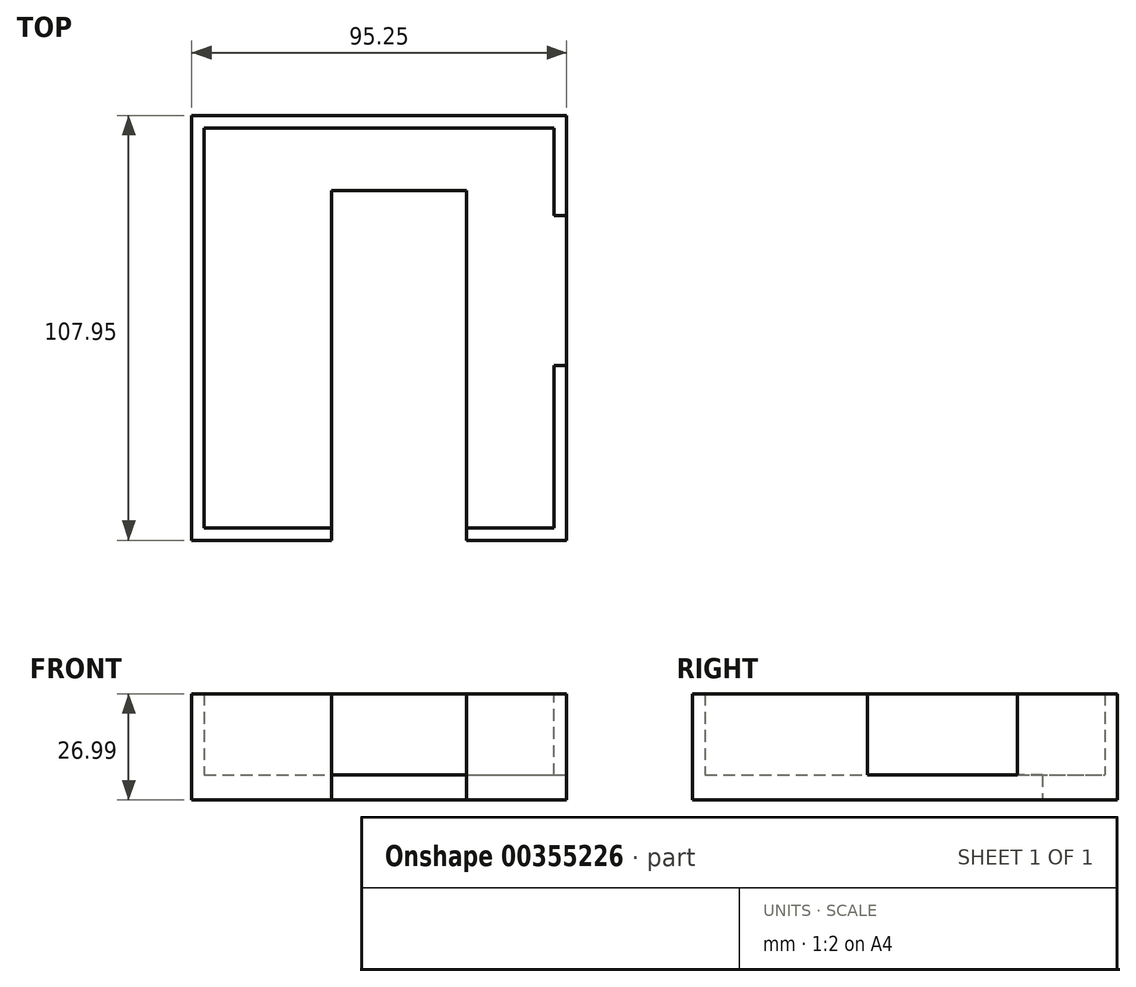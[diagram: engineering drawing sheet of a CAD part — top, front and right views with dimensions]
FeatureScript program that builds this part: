
annotation { "Feature Type Name" : "Feature", "Feature Type Description" : "" }
export const myFeature = defineFeature(function(context is Context, id is Id, definition is map)
    precondition{}
    {
        {
            var Q0;
            Q0=qCreatedBy(makeId("Top.planeOp"),FACE);
            var sketch = newSketch(context, id + "F0", { "sketchPlane" : qUnion([Q0])});
            skLineSegment(sketch, "E0.bottom", {"start": v(-35.56, 52.15) * mm, "end": v(59.7, 52.15) * mm});
            skLineSegment(sketch, "E0.top", {"start": v(-35.56, -55.8) * mm, "end": v(0, -55.8) * mm});
            skLineSegment(sketch, "E0.left", {"start": v(-35.56, 52.15) * mm, "end": v(-35.56, -55.8) * mm});
            skLineSegment(sketch, "E0.right", {"start": v(59.7, 52.15) * mm, "end": v(59.7, -55.8) * mm});
            skPoint(sketch, "E0.middle", {"position": v(12.07, -1.83) * mm});
            skLineSegment(sketch, "E1", {"start": v(34.3, -55.8) * mm, "end": v(34.3, 33.1) * mm});
            skLineSegment(sketch, "E2", {"start": v(34.3, 33.1) * mm, "end": v(0, 33.1) * mm});
            skLineSegment(sketch, "E3", {"start": v(0, 33.1) * mm, "end": v(0, -55.8) * mm});
            skLineSegment(sketch, "E4.trimOffspring", {"start": v(34.3, -55.8) * mm, "end": v(59.7, -55.8) * mm});
            skSolve(sketch);
        }
        {
            var Q0;
            Q0=makeQuery(id+"F0.imprint","IMPRINT",FACE,{"disambiguationData":[TD([[makeQuery(id+"F0.imprint","IMPRINT",EDGE,{"derivedFrom":sQuery(id+"F0.wireOp",EDGE,"E0.bottom")}),-1.0]])]});
            extrude(context, id + "F1", {"entities" : qUnion([Q0]), "depth" : 6.35 * mm});
        }
        {
            var Q0;
            Q0=makeQuery(id+"F1.opExtrude","CAP_FACE",FACE,{"disambiguationData":[OSD([sQuery(id+"F0.wireOp",EDGE,"E0.bottom"),sQuery(id+"F0.wireOp",EDGE,"E0.top"),sQuery(id+"F0.wireOp",EDGE,"E0.left"),sQuery(id+"F0.wireOp",EDGE,"E0.right"),sQuery(id+"F0.wireOp",EDGE,"E1"),sQuery(id+"F0.wireOp",EDGE,"E2"),sQuery(id+"F0.wireOp",EDGE,"E3"),sQuery(id+"F0.wireOp",EDGE,"E4.trimOffspring")])],"isStart":false});
            var sketch = newSketch(context, id + "F2", { "sketchPlane" : qUnion([Q0])});
            skLineSegment(sketch, "E5", {"start": v(0, -55.8) * mm, "end": v(-35.56, -55.8) * mm});
            skLineSegment(sketch, "E6", {"start": v(-35.56, -55.8) * mm, "end": v(-35.56, 52.15) * mm});
            skLineSegment(sketch, "E7", {"start": v(-35.56, 52.15) * mm, "end": v(59.7, 52.15) * mm});
            skLineSegment(sketch, "E8", {"start": v(59.7, 52.15) * mm, "end": v(59.7, -55.8) * mm});
            skLineSegment(sketch, "E9", {"start": v(59.7, -55.8) * mm, "end": v(34.3, -55.8) * mm});
            skLineSegment(sketch, "E10", {"start": v(-32.38, -55.8) * mm, "end": v(-32.39, 52.15) * mm});
            skLineSegment(sketch, "E11", {"start": v(-35.56, -52.63) * mm, "end": v(0, -52.63) * mm});
            skLineSegment(sketch, "E12", {"start": v(34.3, -52.63) * mm, "end": v(59.7, -52.63) * mm});
            skLineSegment(sketch, "E13", {"start": v(56.52, -55.8) * mm, "end": v(56.52, 52.15) * mm});
            skLineSegment(sketch, "E14", {"start": v(-35.56, 48.97) * mm, "end": v(59.7, 48.97) * mm});
            skSolve(sketch);
        }
        {
            var Q0;
            Q0 = qSketchRegion(id + "F2", true);
            var Q1;
            {var subQ0=sQuery(id+"F2.wireOp",EDGE,"E5");var subQ1=makeQuery(id+"F1.opExtrude","CAP_EDGE",EDGE,{"disambiguationData":[OSD([sQuery(id+"F0.wireOp",EDGE,"E3")])],"isStart":false});var subQ2=makeQuery(id+"F2.imprint","INTERSECT",VERTEX,{"derivedFrom":[subQ1,subQ0]});Q1=makeQuery(id+"F2.imprint","IMPRINT",FACE,{"disambiguationData":[TD([[makeQuery(id+"F2.imprint","IMPRINT",EDGE,{"disambiguationData":[TD([[subQ2,1.0]])],"derivedFrom":subQ0}),1.0]])]});}
            var Q2;
            {var subQ0=sQuery(id+"F2.wireOp",EDGE,"E9");var subQ1=makeQuery(id+"F1.opExtrude","CAP_EDGE",EDGE,{"disambiguationData":[OSD([sQuery(id+"F0.wireOp",EDGE,"E1")])],"isStart":false});var subQ2=makeQuery(id+"F2.imprint","INTERSECT",VERTEX,{"derivedFrom":[subQ1,subQ0]});Q2=makeQuery(id+"F2.imprint","IMPRINT",FACE,{"disambiguationData":[TD([[makeQuery(id+"F2.imprint","IMPRINT",EDGE,{"disambiguationData":[TD([[subQ2,-1.0]])],"derivedFrom":subQ0}),1.0]])]});}
            extrude(context, id + "F3", {"entities" : qUnion([Q0, Q1, Q2]), "operationType" : NewBodyOperationType.ADD, "depth" : 20.64 * mm});
        }
        {
            var Q0;
            Q0=makeQuery(id+"F3.boolean.opBoolean","MERGE",FACE,{"derivedFrom":[makeQuery(id+"F1.opExtrude","SWEPT_FACE",FACE,{"disambiguationData":[OSD([sQuery(id+"F0.wireOp",EDGE,"E0.right")])]}),makeQuery(id+"F3.opExtrude","SWEPT_FACE",FACE,{"disambiguationData":[OSD([sQuery(id+"F2.wireOp",EDGE,"E8")])]})]});
            var sketch = newSketch(context, id + "F4", { "sketchPlane" : qUnion([Q0])});
            skLineSegment(sketch, "E15", {"start": v(26.75, 6.35) * mm, "end": v(26.75, 26.99) * mm});
            skLineSegment(sketch, "E16", {"start": v(-11.35, 6.35) * mm, "end": v(-11.35, 26.99) * mm});
            skLineSegment(sketch, "E17", {"start": v(-11.35, 26.99) * mm, "end": v(26.75, 26.99) * mm});
            skLineSegment(sketch, "E18", {"start": v(-11.35, 6.35) * mm, "end": v(26.75, 6.35) * mm});
            skSolve(sketch);
        }
        {
            var Q0;
            Q0=makeQuery(id+"F4.imprint","IMPRINT",FACE,{"disambiguationData":[TD([[makeQuery(id+"F4.imprint","IMPRINT",EDGE,{"derivedFrom":sQuery(id+"F4.wireOp",EDGE,"E15")}),1.0]])]});
            extrude(context, id + "F5", {"entities" : qUnion([Q0]), "operationType" : NewBodyOperationType.REMOVE, "oppositeDirection" : true, "depth" : 3.17 * mm});
        }
    });
